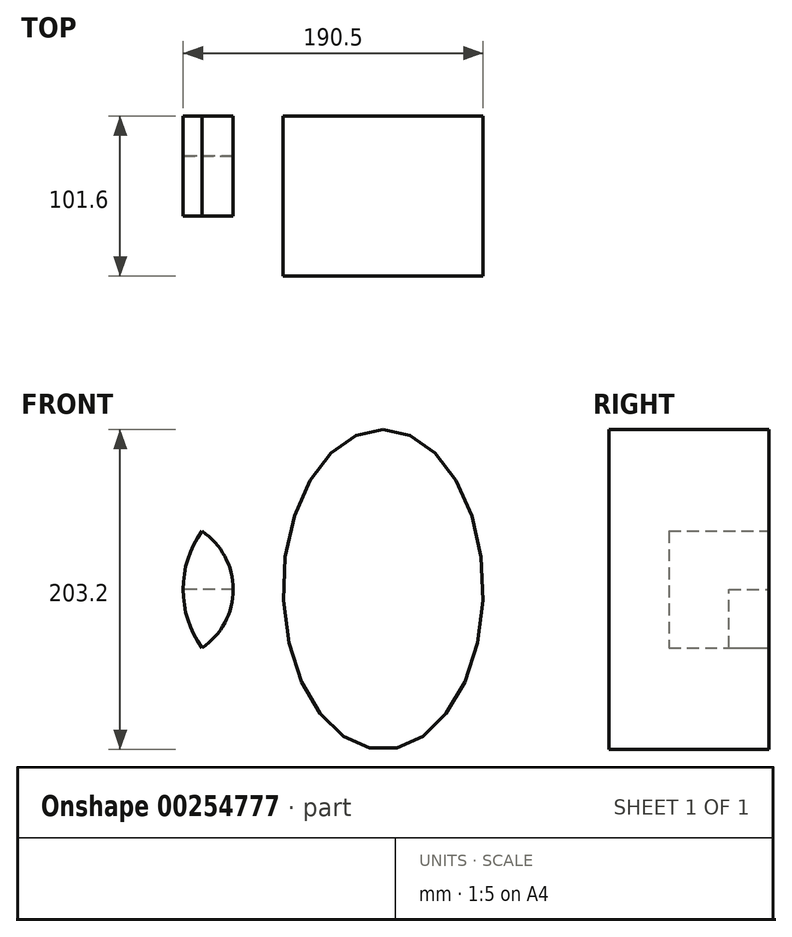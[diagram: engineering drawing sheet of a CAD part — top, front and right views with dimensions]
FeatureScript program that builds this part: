
annotation { "Feature Type Name" : "Feature", "Feature Type Description" : "" }
export const myFeature = defineFeature(function(context is Context, id is Id, definition is map)
    precondition{}
    {
        {
            var Q0;
            Q0=qCreatedBy(makeId("Front.planeOp"),FACE);
            var sketch = newSketch(context, id + "F0", { "sketchPlane" : qUnion([Q0])});
            skLineSegment(sketch, "E0", {"start": v(0, 0) * mm, "end": v(-76.2, 0) * mm});
            skCircle(sketch, "E1", {"center": v(-76.2, 0) * mm, "radius": 44.45 * mm});
            skLineSegment(sketch, "E2", {"start": v(-31.75, 0) * mm, "end": v(-63.5, 0) * mm});
            skCircle(sketch, "E3", {"center": v(0, 0) * mm, "radius": 63.5 * mm});
            skLineSegment(sketch, "E4", {"start": v(63.5, 0) * mm, "end": v(63.5, 101.6) * mm});
            skEllipse(sketch, "E5", {"center": v(63.5, 0) * mm, "majorRadius": 101.6 * mm, "minorRadius": 63.5 * mm, "majorAxis": v(0, 1)});
            skSolve(sketch);
        }
        {
            var Q0;
            {var subQ0=sQuery(id+"F0.wireOp",EDGE,"E3");var subQ1=sQuery(id+"F0.wireOp",EDGE,"E1");var subQ2=makeQuery(id+"F0.imprint","INTERSECT",VERTEX,{"disambiguationData":[OD(0.0)],"derivedFrom":[subQ1,subQ0]});Q0=makeQuery(id+"F0.imprint","IMPRINT",FACE,{"disambiguationData":[TD([[makeQuery(id+"F0.imprint","IMPRINT",EDGE,{"disambiguationData":[TD([[subQ2,-1.0]])],"derivedFrom":subQ1}),1.0]])]});}
            extrude(context, id + "F1", {"entities" : qUnion([Q0]), "depth" : 25.4 * mm});
        }
        {
            var Q0;
            {var subQ3=sQuery(id+"F0.wireOp",EDGE,"E1");var subQ5=sQuery(id+"F0.wireOp",EDGE,"E3");var subQ6=makeQuery(id+"F0.imprint","INTERSECT",VERTEX,{"disambiguationData":[OD(1.0)],"derivedFrom":[subQ3,subQ5]});Q0=makeQuery(id+"F0.imprint","IMPRINT",FACE,{"disambiguationData":[TD([[makeQuery(id+"F0.imprint","IMPRINT",EDGE,{"disambiguationData":[TD([[subQ6,-1.0]])],"derivedFrom":subQ5}),1.0]])]});}
            var Q1;
            {var subQ3=sQuery(id+"F0.wireOp",EDGE,"E1");var subQ5=sQuery(id+"F0.wireOp",EDGE,"E3");var subQ6=makeQuery(id+"F0.imprint","INTERSECT",VERTEX,{"disambiguationData":[OD(0.0)],"derivedFrom":[subQ3,subQ5]});Q1=makeQuery(id+"F0.imprint","IMPRINT",FACE,{"disambiguationData":[TD([[makeQuery(id+"F0.imprint","IMPRINT",EDGE,{"disambiguationData":[TD([[subQ6,1.0]])],"derivedFrom":subQ5}),1.0]])]});}
            var Q2;
            {var subQ0=sQuery(id+"F0.wireOp",EDGE,"E2");Q2=makeQuery(id+"F0.imprint","IMPRINT",FACE,{"disambiguationData":[TD([[makeQuery(id+"F0.imprint","IMPRINT",EDGE,{"derivedFrom":subQ0}),-1.0]])]});}
            var Q3;
            {var subQ0=sQuery(id+"F0.wireOp",EDGE,"E2");Q3=makeQuery(id+"F0.imprint","IMPRINT",FACE,{"disambiguationData":[TD([[makeQuery(id+"F0.imprint","IMPRINT",EDGE,{"derivedFrom":subQ0}),1.0]])]});}
            extrude(context, id + "F2", {"entities" : qUnion([Q0, Q1, Q2, Q3]), "depth" : 63.5 * mm});
        }
        {
            var Q0;
            {var subQ0=sQuery(id+"F0.wireOp",EDGE,"E4");Q0=makeQuery(id+"F0.imprint","IMPRINT",FACE,{"disambiguationData":[TD([[makeQuery(id+"F0.imprint","IMPRINT",EDGE,{"derivedFrom":subQ0}),1.0]])]});}
            var Q1;
            {var subQ0=sQuery(id+"F0.wireOp",EDGE,"E4");Q1=makeQuery(id+"F0.imprint","IMPRINT",FACE,{"disambiguationData":[TD([[makeQuery(id+"F0.imprint","IMPRINT",EDGE,{"derivedFrom":subQ0}),-1.0]])]});}
            var Q2;
            {var subQ0=sQuery(id+"F0.wireOp",EDGE,"E3");var subQ1=makeQuery(id+"F0.imprint","INTERSECT",VERTEX,{"derivedFrom":[subQ0,sQuery(id+"F0.wireOp",EDGE,"E4")]});Q2=makeQuery(id+"F0.imprint","IMPRINT",FACE,{"disambiguationData":[TD([[makeQuery(id+"F0.imprint","IMPRINT",EDGE,{"disambiguationData":[TD([[subQ1,-1.0]])],"derivedFrom":subQ0}),1.0]])]});}
            extrude(context, id + "F3", {"entities" : qUnion([Q0, Q1, Q2]), "depth" : 101.6 * mm});
        }
    });
